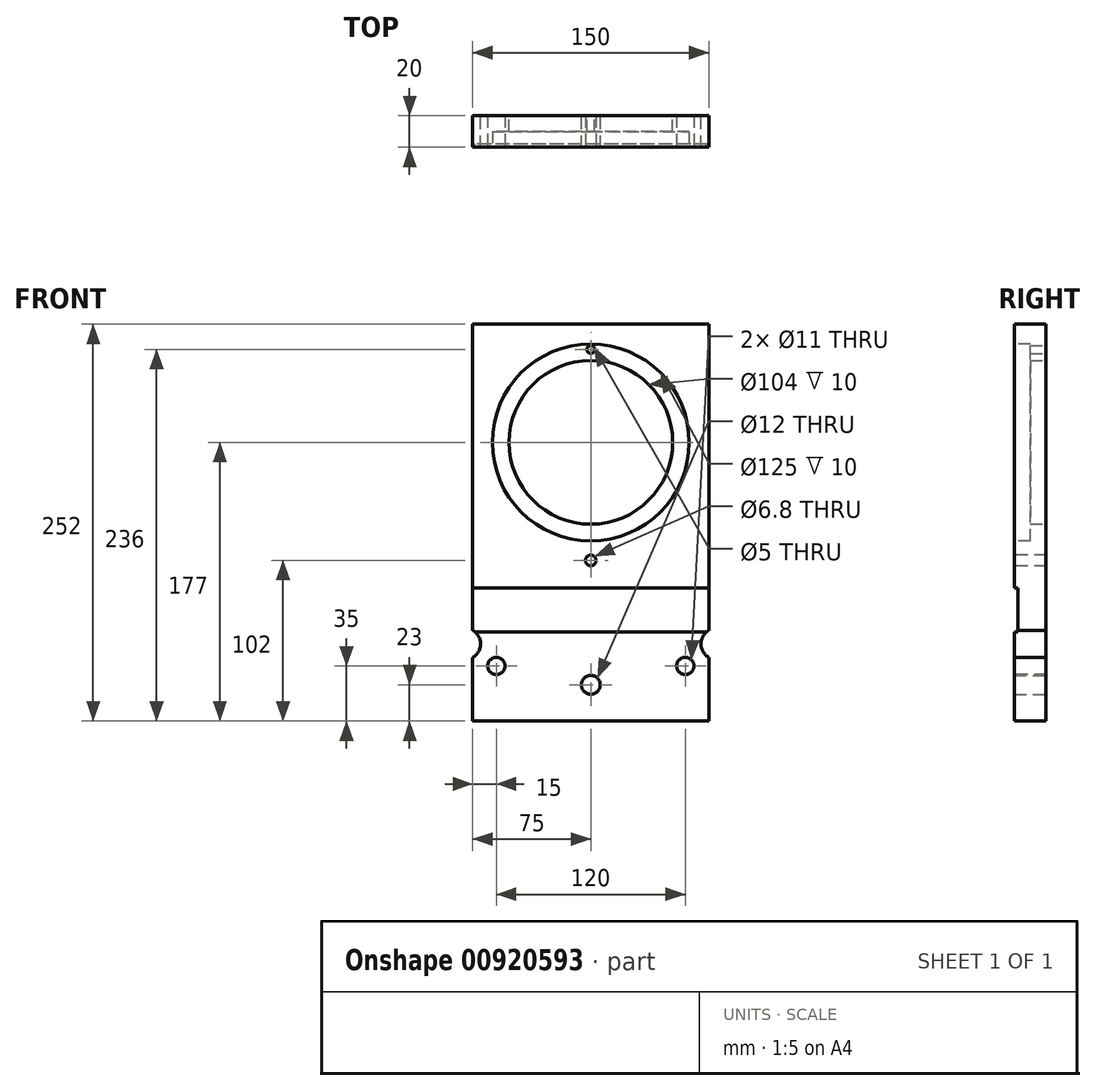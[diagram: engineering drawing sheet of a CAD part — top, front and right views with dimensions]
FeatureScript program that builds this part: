
annotation { "Feature Type Name" : "Feature", "Feature Type Description" : "" }
export const myFeature = defineFeature(function(context is Context, id is Id, definition is map)
    precondition{}
    {
        {
            var Q0;
            Q0=qCreatedBy(makeId("Front.planeOp"),FACE);
            var sketch = newSketch(context, id + "F0", { "sketchPlane" : qUnion([Q0])});
            skLineSegment(sketch, "E0.bottom", {"start": v(-75, -60) * mm, "end": v(-35, -60) * mm, "construction": true});
            skLineSegment(sketch, "E0.top", {"start": v(-75, 30) * mm, "end": v(75, 30) * mm});
            skLineSegment(sketch, "E0.left", {"start": v(-75, -60) * mm, "end": v(-75, 30) * mm});
            skLineSegment(sketch, "E0.right", {"start": v(75, -60) * mm, "end": v(75, 30) * mm});
            skLineSegment(sketch, "E1", {"start": v(-35, -60) * mm, "end": v(-35, -10) * mm, "construction": true});
            skLineSegment(sketch, "E2", {"start": v(-35, -10) * mm, "end": v(35, -10) * mm, "construction": true});
            skLineSegment(sketch, "E3", {"start": v(35, -10) * mm, "end": v(35, -60) * mm, "construction": true});
            skLineSegment(sketch, "E4.trimOffspring", {"start": v(35, -60) * mm, "end": v(75, -60) * mm, "construction": true});
            skLineSegment(sketch, "E5", {"start": v(-75, -60) * mm, "end": v(75, -60) * mm});
            skSolve(sketch);
        }
        {
            var Q0;
            Q0=makeQuery(id+"F0.imprint","IMPRINT",FACE,{"disambiguationData":[TD([[makeQuery(id+"F0.imprint","IMPRINT",EDGE,{"derivedFrom":sQuery(id+"F0.wireOp",EDGE,"E0.top")}),-1.0]])]});
            extrude(context, id + "F1", {"entities" : qUnion([Q0]), "depth" : 20 * mm, "offsetDistance" : 25 * mm});
        }
        {
            var Q0;
            Q0=makeQuery(id+"F1.opExtrude","CAP_FACE",FACE,{"disambiguationData":[OSD([sQuery(id+"F0.wireOp",EDGE,"E0.bottom"),sQuery(id+"F0.wireOp",EDGE,"E0.top"),sQuery(id+"F0.wireOp",EDGE,"E0.left"),sQuery(id+"F0.wireOp",EDGE,"E0.right"),sQuery(id+"F0.wireOp",EDGE,"E1"),sQuery(id+"F0.wireOp",EDGE,"E2"),sQuery(id+"F0.wireOp",EDGE,"E3"),sQuery(id+"F0.wireOp",EDGE,"E4.trimOffspring")])],"isStart":false});
            var sketch = newSketch(context, id + "F2", { "sketchPlane" : qUnion([Q0])});
            skCircle(sketch, "E6", {"center": v(-60, -45) * mm, "radius": 5.5 * mm});
            skCircle(sketch, "E7", {"center": v(60, -45) * mm, "radius": 5.5 * mm});
            skSolve(sketch);
        }
        {
            var Q0;
            Q0=makeQuery(id+"F2.imprint","IMPRINT",FACE,{"disambiguationData":[TD([[makeQuery(id+"F2.imprint","IMPRINT",EDGE,{"derivedFrom":sQuery(id+"F2.wireOp",EDGE,"E6")}),1.0]])]});
            var Q1;
            Q1=makeQuery(id+"F2.imprint","IMPRINT",FACE,{"disambiguationData":[TD([[makeQuery(id+"F2.imprint","IMPRINT",EDGE,{"derivedFrom":sQuery(id+"F2.wireOp",EDGE,"E7")}),1.0]])]});
            extrude(context, id + "F3", {"entities" : qUnion([Q0, Q1]), "operationType" : NewBodyOperationType.REMOVE, "endBound" : BoundingType.THROUGH_ALL, "oppositeDirection" : true, "depth" : 25 * mm, "offsetDistance" : 25 * mm});
        }
        {
            var Q0;
            Q0=makeQuery(id+"F1.opExtrude","SWEPT_FACE",FACE,{"disambiguationData":[OSD([sQuery(id+"F0.wireOp",EDGE,"E0.left")])]});
            var sketch = newSketch(context, id + "F4", { "sketchPlane" : qUnion([Q0])});
            skLineSegment(sketch, "E8.bottom", {"start": v(20, 4.5) * mm, "end": v(18, 4.5) * mm});
            skLineSegment(sketch, "E8.top", {"start": v(20, -23.5) * mm, "end": v(18, -23.5) * mm});
            skLineSegment(sketch, "E8.left", {"start": v(20, 4.5) * mm, "end": v(20, -23.5) * mm});
            skLineSegment(sketch, "E8.right", {"start": v(18, 4.5) * mm, "end": v(18, -23.5) * mm});
            skSolve(sketch);
        }
        {
            var Q0;
            Q0=makeQuery(id+"F4.imprint","IMPRINT",FACE,{"disambiguationData":[TD([[makeQuery(id+"F4.imprint","IMPRINT",EDGE,{"derivedFrom":sQuery(id+"F4.wireOp",EDGE,"E8.bottom")}),1.0]])]});
            extrude(context, id + "F5", {"entities" : qUnion([Q0]), "operationType" : NewBodyOperationType.REMOVE, "endBound" : BoundingType.THROUGH_ALL, "oppositeDirection" : true, "depth" : 25 * mm, "offsetDistance" : 25 * mm});
        }
        {
            var Q0;
            Q0=makeQuery(id+"F1.opExtrude","CAP_FACE",FACE,{"disambiguationData":[OSD([sQuery(id+"F0.wireOp",EDGE,"E0.bottom"),sQuery(id+"F0.wireOp",EDGE,"E0.top"),sQuery(id+"F0.wireOp",EDGE,"E0.left"),sQuery(id+"F0.wireOp",EDGE,"E0.right"),sQuery(id+"F0.wireOp",EDGE,"E1"),sQuery(id+"F0.wireOp",EDGE,"E2"),sQuery(id+"F0.wireOp",EDGE,"E3"),sQuery(id+"F0.wireOp",EDGE,"E4.trimOffspring")])],"isStart":true});
            var sketch = newSketch(context, id + "F6", { "sketchPlane" : qUnion([Q0])});
            skLineSegment(sketch, "E9", {"start": v(-75, 30) * mm, "end": v(-20, 154) * mm, "construction": true});
            skLineSegment(sketch, "E10", {"start": v(-75, 154) * mm, "end": v(75, 154) * mm});
            skLineSegment(sketch, "E11", {"start": v(20, 154) * mm, "end": v(75, 30) * mm, "construction": true});
            skLineSegment(sketch, "E12", {"start": v(75, 30) * mm, "end": v(-75, 30) * mm});
            skCircle(sketch, "E13", {"center": v(0, 97) * mm, "radius": 30 * mm});
            skLineSegment(sketch, "E14", {"start": v(75, 30) * mm, "end": v(75, 154) * mm});
            skLineSegment(sketch, "E15", {"start": v(-75, 30) * mm, "end": v(-75, 154) * mm});
            skSolve(sketch);
        }
        {
            var Q0;
            Q0=makeQuery(id+"F6.imprint","IMPRINT",FACE,{"disambiguationData":[TD([[makeQuery(id+"F6.imprint","IMPRINT",EDGE,{"derivedFrom":sQuery(id+"F6.wireOp",EDGE,"E10")}),-1.0]])]});
            extrude(context, id + "F7", {"entities" : qUnion([Q0]), "operationType" : NewBodyOperationType.ADD, "oppositeDirection" : true, "depth" : 20 * mm, "offsetDistance" : 25 * mm});
        }
        {
            var Q0;
            Q0=makeQuery(id+"F7.boolean.opBoolean","MERGE",FACE,{"derivedFrom":[makeQuery(id+"F1.opExtrude","CAP_FACE",FACE,{"disambiguationData":[OSD([sQuery(id+"F0.wireOp",EDGE,"E0.bottom"),sQuery(id+"F0.wireOp",EDGE,"E0.top"),sQuery(id+"F0.wireOp",EDGE,"E0.left"),sQuery(id+"F0.wireOp",EDGE,"E0.right"),sQuery(id+"F0.wireOp",EDGE,"E1"),sQuery(id+"F0.wireOp",EDGE,"E2"),sQuery(id+"F0.wireOp",EDGE,"E3"),sQuery(id+"F0.wireOp",EDGE,"E4.trimOffspring")])],"isStart":true}),makeQuery(id+"F7.opExtrude","CAP_FACE",FACE,{"disambiguationData":[OSD([sQuery(id+"F6.wireOp",EDGE,"E10"),sQuery(id+"F6.wireOp",EDGE,"E12"),sQuery(id+"F6.wireOp",EDGE,"E13"),sQuery(id+"F6.wireOp",EDGE,"E14"),sQuery(id+"F6.wireOp",EDGE,"E15")])],"isStart":true})]});
            var sketch = newSketch(context, id + "F8", { "sketchPlane" : qUnion([Q0])});
            skCircle(sketch, "E16", {"center": v(-80, -31) * mm, "radius": 10 * mm});
            skCircle(sketch, "E17", {"center": v(80, -31) * mm, "radius": 10 * mm});
            skSolve(sketch);
        }
        {
            var Q0;
            {var subQ0=sQuery(id+"F8.wireOp",EDGE,"E16");var subQ1=makeQuery(id+"F7.boolean.opBoolean","MERGE",EDGE,{"derivedFrom":[makeQuery(id+"F1.opExtrude","CAP_EDGE",EDGE,{"disambiguationData":[OSD([sQuery(id+"F0.wireOp",EDGE,"E0.right")])],"isStart":true}),makeQuery(id+"F7.opExtrude","CAP_EDGE",EDGE,{"disambiguationData":[OSD([sQuery(id+"F6.wireOp",EDGE,"E15")])],"isStart":true})]});var subQ2=makeQuery(id+"F8.imprint","INTERSECT",VERTEX,{"disambiguationData":[OD(0.0)],"derivedFrom":[subQ1,subQ0]});Q0=makeQuery(id+"F8.imprint","IMPRINT",FACE,{"disambiguationData":[TD([[makeQuery(id+"F8.imprint","IMPRINT",EDGE,{"disambiguationData":[TD([[subQ2,1.0]])],"derivedFrom":subQ0}),1.0]])]});}
            var Q1;
            {var subQ0=sQuery(id+"F8.wireOp",EDGE,"E16");var subQ1=makeQuery(id+"F7.boolean.opBoolean","MERGE",EDGE,{"derivedFrom":[makeQuery(id+"F1.opExtrude","CAP_EDGE",EDGE,{"disambiguationData":[OSD([sQuery(id+"F0.wireOp",EDGE,"E0.right")])],"isStart":true}),makeQuery(id+"F7.opExtrude","CAP_EDGE",EDGE,{"disambiguationData":[OSD([sQuery(id+"F6.wireOp",EDGE,"E15")])],"isStart":true})]});var subQ2=makeQuery(id+"F8.imprint","INTERSECT",VERTEX,{"disambiguationData":[OD(0.0)],"derivedFrom":[subQ1,subQ0]});Q1=makeQuery(id+"F8.imprint","IMPRINT",FACE,{"disambiguationData":[TD([[makeQuery(id+"F8.imprint","IMPRINT",EDGE,{"disambiguationData":[TD([[subQ2,-1.0]])],"derivedFrom":subQ0}),1.0]])]});}
            var Q2;
            {var subQ0=sQuery(id+"F8.wireOp",EDGE,"E17");var subQ1=makeQuery(id+"F7.boolean.opBoolean","MERGE",EDGE,{"derivedFrom":[makeQuery(id+"F1.opExtrude","CAP_EDGE",EDGE,{"disambiguationData":[OSD([sQuery(id+"F0.wireOp",EDGE,"E0.left")])],"isStart":true}),makeQuery(id+"F7.opExtrude","CAP_EDGE",EDGE,{"disambiguationData":[OSD([sQuery(id+"F6.wireOp",EDGE,"E14")])],"isStart":true})]});var subQ2=makeQuery(id+"F8.imprint","INTERSECT",VERTEX,{"disambiguationData":[OD(0.0)],"derivedFrom":[subQ1,subQ0]});Q2=makeQuery(id+"F8.imprint","IMPRINT",FACE,{"disambiguationData":[TD([[makeQuery(id+"F8.imprint","IMPRINT",EDGE,{"disambiguationData":[TD([[subQ2,1.0]])],"derivedFrom":subQ0}),1.0]])]});}
            var Q3;
            {var subQ0=sQuery(id+"F8.wireOp",EDGE,"E17");var subQ1=makeQuery(id+"F7.boolean.opBoolean","MERGE",EDGE,{"derivedFrom":[makeQuery(id+"F1.opExtrude","CAP_EDGE",EDGE,{"disambiguationData":[OSD([sQuery(id+"F0.wireOp",EDGE,"E0.left")])],"isStart":true}),makeQuery(id+"F7.opExtrude","CAP_EDGE",EDGE,{"disambiguationData":[OSD([sQuery(id+"F6.wireOp",EDGE,"E14")])],"isStart":true})]});var subQ2=makeQuery(id+"F8.imprint","INTERSECT",VERTEX,{"disambiguationData":[OD(0.0)],"derivedFrom":[subQ1,subQ0]});Q3=makeQuery(id+"F8.imprint","IMPRINT",FACE,{"disambiguationData":[TD([[makeQuery(id+"F8.imprint","IMPRINT",EDGE,{"disambiguationData":[TD([[subQ2,-1.0]])],"derivedFrom":subQ0}),1.0]])]});}
            extrude(context, id + "F9", {"entities" : qUnion([Q0, Q1, Q2, Q3]), "operationType" : NewBodyOperationType.REMOVE, "endBound" : BoundingType.THROUGH_ALL, "oppositeDirection" : true, "depth" : 25 * mm, "offsetDistance" : 25 * mm});
        }
        {
            var Q0;
            {var subQ0=sQuery(id+"F0.wireOp",EDGE,"E0.top");var subQ1=sQuery(id+"F0.wireOp",EDGE,"E0.left");var subQ2=sQuery(id+"F0.wireOp",EDGE,"E0.right");Q0=makeQuery(id+"F7.boolean.opBoolean","MERGE",FACE,{"derivedFrom":[makeQuery(id+"F5.boolean.opBoolean","SPLIT",FACE,{"disambiguationData":[TD([makeQuery(id+"F1.opExtrude","SWEPT_FACE",FACE,{"disambiguationData":[OSD([subQ0])]})])],"derivedFrom":makeQuery(id+"F1.opExtrude","CAP_FACE",FACE,{"disambiguationData":[OSD([subQ0,subQ1,subQ2,sQuery(id+"F0.wireOp",EDGE,"E5")])],"isStart":false})}),makeQuery(id+"F7.opExtrude","CAP_FACE",FACE,{"disambiguationData":[OSD([sQuery(id+"F6.wireOp",EDGE,"E10"),sQuery(id+"F6.wireOp",EDGE,"E12"),sQuery(id+"F6.wireOp",EDGE,"E13"),sQuery(id+"F6.wireOp",EDGE,"E14"),sQuery(id+"F6.wireOp",EDGE,"E15")])],"isStart":false})]});}
            var sketch = newSketch(context, id + "F10", { "sketchPlane" : qUnion([Q0])});
            skCircle(sketch, "E18.0", {"center": v(0, 97) * mm, "radius": 30 * mm, "construction": true});
            skLineSegment(sketch, "E19.bottom", {"start": v(-3.5, 146) * mm, "end": v(3.5, 146) * mm});
            skLineSegment(sketch, "E19.top", {"start": v(-3.5, 128) * mm, "end": v(3.5, 128) * mm});
            skLineSegment(sketch, "E19.left", {"start": v(-3.5, 146) * mm, "end": v(-3.5, 128) * mm});
            skLineSegment(sketch, "E19.right", {"start": v(3.5, 146) * mm, "end": v(3.5, 128) * mm});
            skLineSegment(sketch, "E20", {"start": v(-3.5, 137) * mm, "end": v(3.5, 137) * mm, "construction": true});
            skSolve(sketch);
        }
        {
            var Q0;
            Q0=makeQuery(id+"F7.boolean.opBoolean","MERGE",FACE,{"derivedFrom":[makeQuery(id+"F1.opExtrude","CAP_FACE",FACE,{"disambiguationData":[OSD([sQuery(id+"F0.wireOp",EDGE,"E0.top"),sQuery(id+"F0.wireOp",EDGE,"E0.left"),sQuery(id+"F0.wireOp",EDGE,"E0.right"),sQuery(id+"F0.wireOp",EDGE,"E5")])],"isStart":true}),makeQuery(id+"F7.opExtrude","CAP_FACE",FACE,{"disambiguationData":[OSD([sQuery(id+"F6.wireOp",EDGE,"E10"),sQuery(id+"F6.wireOp",EDGE,"E12"),sQuery(id+"F6.wireOp",EDGE,"E13"),sQuery(id+"F6.wireOp",EDGE,"E14"),sQuery(id+"F6.wireOp",EDGE,"E15")])],"isStart":true})]});
            var sketch = newSketch(context, id + "F11", { "sketchPlane" : qUnion([Q0])});
            skLineSegment(sketch, "E21.bottom", {"start": v(-75, -60) * mm, "end": v(75, -60) * mm});
            skLineSegment(sketch, "E21.top", {"start": v(-75, -80) * mm, "end": v(75, -80) * mm});
            skLineSegment(sketch, "E21.left", {"start": v(-75, -60) * mm, "end": v(-75, -80) * mm});
            skLineSegment(sketch, "E21.right", {"start": v(75, -60) * mm, "end": v(75, -80) * mm});
            skPoint(sketch, "E22.centerSnap0", {"position": v(0, -60) * mm});
            skSolve(sketch);
        }
        {
            var Q0;
            Q0=makeQuery(id+"F11.imprint","IMPRINT",FACE,{"disambiguationData":[TD([[makeQuery(id+"F11.imprint","IMPRINT",EDGE,{"derivedFrom":sQuery(id+"F11.wireOp",EDGE,"E21.bottom")}),1.0]])]});
            extrude(context, id + "F12", {"entities" : qUnion([Q0]), "operationType" : NewBodyOperationType.ADD, "oppositeDirection" : true, "depth" : 20 * mm, "offsetDistance" : 25 * mm});
        }
        {
            var Q0;
            Q0=makeQuery(id+"F12.boolean.opBoolean","MERGE",FACE,{"derivedFrom":[makeQuery(id+"F7.boolean.opBoolean","MERGE",FACE,{"derivedFrom":[makeQuery(id+"F1.opExtrude","CAP_FACE",FACE,{"disambiguationData":[OSD([sQuery(id+"F0.wireOp",EDGE,"E0.top"),sQuery(id+"F0.wireOp",EDGE,"E0.left"),sQuery(id+"F0.wireOp",EDGE,"E0.right"),sQuery(id+"F0.wireOp",EDGE,"E5")])],"isStart":true}),makeQuery(id+"F7.opExtrude","CAP_FACE",FACE,{"disambiguationData":[OSD([sQuery(id+"F6.wireOp",EDGE,"E10"),sQuery(id+"F6.wireOp",EDGE,"E12"),sQuery(id+"F6.wireOp",EDGE,"E13"),sQuery(id+"F6.wireOp",EDGE,"E14"),sQuery(id+"F6.wireOp",EDGE,"E15")])],"isStart":true})]}),makeQuery(id+"F12.opExtrude","CAP_FACE",FACE,{"disambiguationData":[OSD([sQuery(id+"F11.wireOp",EDGE,"E21.bottom"),sQuery(id+"F11.wireOp",EDGE,"E21.top"),sQuery(id+"F11.wireOp",EDGE,"E21.left"),sQuery(id+"F11.wireOp",EDGE,"E21.right")])],"isStart":true})]});
            var sketch = newSketch(context, id + "F13", { "sketchPlane" : qUnion([Q0])});
            skCircle(sketch, "E23", {"center": v(0, -57) * mm, "radius": 6 * mm});
            skCircle(sketch, "E24.0", {"center": v(0, 97) * mm, "radius": 30 * mm, "construction": true});
            skSolve(sketch);
        }
        {
            var Q0;
            Q0=makeQuery(id+"F13.imprint","IMPRINT",FACE,{"disambiguationData":[TD([[makeQuery(id+"F13.imprint","IMPRINT",EDGE,{"derivedFrom":sQuery(id+"F13.wireOp",EDGE,"E23")}),1.0]])]});
            extrude(context, id + "F14", {"entities" : qUnion([Q0]), "operationType" : NewBodyOperationType.REMOVE, "endBound" : BoundingType.THROUGH_ALL, "oppositeDirection" : true, "depth" : 25 * mm, "offsetDistance" : 25 * mm});
        }
        {
            var Q0;
            {var subQ0=sQuery(id+"F0.wireOp",EDGE,"E0.top");var subQ1=sQuery(id+"F0.wireOp",EDGE,"E0.left");var subQ2=sQuery(id+"F0.wireOp",EDGE,"E0.right");Q0=makeQuery(id+"F7.boolean.opBoolean","MERGE",FACE,{"derivedFrom":[makeQuery(id+"F5.boolean.opBoolean","SPLIT",FACE,{"disambiguationData":[TD([makeQuery(id+"F1.opExtrude","SWEPT_FACE",FACE,{"disambiguationData":[OSD([subQ0])]})])],"derivedFrom":makeQuery(id+"F1.opExtrude","CAP_FACE",FACE,{"disambiguationData":[OSD([subQ0,subQ1,subQ2,sQuery(id+"F0.wireOp",EDGE,"E5")])],"isStart":false})}),makeQuery(id+"F7.opExtrude","CAP_FACE",FACE,{"disambiguationData":[OSD([sQuery(id+"F6.wireOp",EDGE,"E10"),sQuery(id+"F6.wireOp",EDGE,"E12"),sQuery(id+"F6.wireOp",EDGE,"E13"),sQuery(id+"F6.wireOp",EDGE,"E14"),sQuery(id+"F6.wireOp",EDGE,"E15")])],"isStart":false})]});}
            var sketch = newSketch(context, id + "F15", { "sketchPlane" : qUnion([Q0])});
            skLineSegment(sketch, "E25.bottom", {"start": v(-75, 154) * mm, "end": v(75, 154) * mm});
            skLineSegment(sketch, "E25.top", {"start": v(-75, 172) * mm, "end": v(75, 172) * mm});
            skLineSegment(sketch, "E25.left", {"start": v(-75, 154) * mm, "end": v(-75, 172) * mm});
            skLineSegment(sketch, "E25.right", {"start": v(75, 154) * mm, "end": v(75, 172) * mm});
            skSolve(sketch);
        }
        {
            var Q0;
            Q0=makeQuery(id+"F15.imprint","IMPRINT",FACE,{"disambiguationData":[TD([[makeQuery(id+"F15.imprint","IMPRINT",EDGE,{"derivedFrom":sQuery(id+"F15.wireOp",EDGE,"E25.bottom")}),-1.0]])]});
            extrude(context, id + "F16", {"entities" : qUnion([Q0]), "operationType" : NewBodyOperationType.ADD, "oppositeDirection" : true, "depth" : 20 * mm, "offsetDistance" : 25 * mm});
        }
        {
            var Q0;
            Q0=makeQuery(id+"F16.boolean.opBoolean","MERGE",FACE,{"derivedFrom":[makeQuery(id+"F12.boolean.opBoolean","MERGE",FACE,{"derivedFrom":[makeQuery(id+"F7.boolean.opBoolean","MERGE",FACE,{"derivedFrom":[makeQuery(id+"F1.opExtrude","CAP_FACE",FACE,{"disambiguationData":[OSD([sQuery(id+"F0.wireOp",EDGE,"E0.top"),sQuery(id+"F0.wireOp",EDGE,"E0.left"),sQuery(id+"F0.wireOp",EDGE,"E0.right"),sQuery(id+"F0.wireOp",EDGE,"E5")])],"isStart":true}),makeQuery(id+"F7.opExtrude","CAP_FACE",FACE,{"disambiguationData":[OSD([sQuery(id+"F6.wireOp",EDGE,"E10"),sQuery(id+"F6.wireOp",EDGE,"E12"),sQuery(id+"F6.wireOp",EDGE,"E13"),sQuery(id+"F6.wireOp",EDGE,"E14"),sQuery(id+"F6.wireOp",EDGE,"E15")])],"isStart":true})]}),makeQuery(id+"F12.opExtrude","CAP_FACE",FACE,{"disambiguationData":[OSD([sQuery(id+"F11.wireOp",EDGE,"E21.bottom"),sQuery(id+"F11.wireOp",EDGE,"E21.top"),sQuery(id+"F11.wireOp",EDGE,"E21.left"),sQuery(id+"F11.wireOp",EDGE,"E21.right")])],"isStart":true})]}),makeQuery(id+"F16.opExtrude","CAP_FACE",FACE,{"disambiguationData":[OSD([sQuery(id+"F15.wireOp",EDGE,"E25.bottom"),sQuery(id+"F15.wireOp",EDGE,"E25.top"),sQuery(id+"F15.wireOp",EDGE,"E25.left"),sQuery(id+"F15.wireOp",EDGE,"E25.right")])],"isStart":false})]});
            var sketch = newSketch(context, id + "F17", { "sketchPlane" : qUnion([Q0])});
            skCircle(sketch, "E26", {"center": v(0, 97) * mm, "radius": 52 * mm});
            skSolve(sketch);
        }
        {
            var Q0;
            Q0=makeQuery(id+"F17.imprint","IMPRINT",FACE,{"disambiguationData":[TD([[makeQuery(id+"F17.imprint","IMPRINT",EDGE,{"derivedFrom":sQuery(id+"F17.wireOp",EDGE,"E26")}),1.0]])]});
            extrude(context, id + "F18", {"entities" : qUnion([Q0]), "operationType" : NewBodyOperationType.REMOVE, "oppositeDirection" : true, "depth" : 20 * mm, "offsetDistance" : 25 * mm});
        }
        {
            var Q0;
            Q0=makeQuery(id+"F16.boolean.opBoolean","MERGE",FACE,{"derivedFrom":[makeQuery(id+"F12.boolean.opBoolean","MERGE",FACE,{"derivedFrom":[makeQuery(id+"F7.boolean.opBoolean","MERGE",FACE,{"derivedFrom":[makeQuery(id+"F1.opExtrude","CAP_FACE",FACE,{"disambiguationData":[OSD([sQuery(id+"F0.wireOp",EDGE,"E0.top"),sQuery(id+"F0.wireOp",EDGE,"E0.left"),sQuery(id+"F0.wireOp",EDGE,"E0.right"),sQuery(id+"F0.wireOp",EDGE,"E5")])],"isStart":true}),makeQuery(id+"F7.opExtrude","CAP_FACE",FACE,{"disambiguationData":[OSD([sQuery(id+"F6.wireOp",EDGE,"E10"),sQuery(id+"F6.wireOp",EDGE,"E12"),sQuery(id+"F6.wireOp",EDGE,"E13"),sQuery(id+"F6.wireOp",EDGE,"E14"),sQuery(id+"F6.wireOp",EDGE,"E15")])],"isStart":true})]}),makeQuery(id+"F12.opExtrude","CAP_FACE",FACE,{"disambiguationData":[OSD([sQuery(id+"F11.wireOp",EDGE,"E21.bottom"),sQuery(id+"F11.wireOp",EDGE,"E21.top"),sQuery(id+"F11.wireOp",EDGE,"E21.left"),sQuery(id+"F11.wireOp",EDGE,"E21.right")])],"isStart":true})]}),makeQuery(id+"F16.opExtrude","CAP_FACE",FACE,{"disambiguationData":[OSD([sQuery(id+"F15.wireOp",EDGE,"E25.bottom"),sQuery(id+"F15.wireOp",EDGE,"E25.top"),sQuery(id+"F15.wireOp",EDGE,"E25.left"),sQuery(id+"F15.wireOp",EDGE,"E25.right")])],"isStart":false})]});
            var sketch = newSketch(context, id + "F19", { "sketchPlane" : qUnion([Q0])});
            skLineSegment(sketch, "E27.bottom", {"start": v(-75, -80) * mm, "end": v(75, -80) * mm});
            skLineSegment(sketch, "E27.top", {"start": v(-75, -113.5) * mm, "end": v(75, -113.5) * mm});
            skLineSegment(sketch, "E27.left", {"start": v(-75, -80) * mm, "end": v(-75, -113.5) * mm});
            skLineSegment(sketch, "E27.right", {"start": v(75, -80) * mm, "end": v(75, -113.5) * mm});
            skSolve(sketch);
        }
        {
            var Q0;
            {var subQ0=sQuery(id+"F0.wireOp",EDGE,"E0.top");var subQ1=sQuery(id+"F0.wireOp",EDGE,"E0.left");var subQ2=sQuery(id+"F0.wireOp",EDGE,"E0.right");Q0=makeQuery(id+"F16.boolean.opBoolean","MERGE",FACE,{"derivedFrom":[makeQuery(id+"F7.boolean.opBoolean","MERGE",FACE,{"derivedFrom":[makeQuery(id+"F5.boolean.opBoolean","SPLIT",FACE,{"disambiguationData":[TD([makeQuery(id+"F1.opExtrude","SWEPT_FACE",FACE,{"disambiguationData":[OSD([subQ0])]})])],"derivedFrom":makeQuery(id+"F1.opExtrude","CAP_FACE",FACE,{"disambiguationData":[OSD([subQ0,subQ1,subQ2,sQuery(id+"F0.wireOp",EDGE,"E5")])],"isStart":false})}),makeQuery(id+"F7.opExtrude","CAP_FACE",FACE,{"disambiguationData":[OSD([sQuery(id+"F6.wireOp",EDGE,"E10"),sQuery(id+"F6.wireOp",EDGE,"E12"),sQuery(id+"F6.wireOp",EDGE,"E13"),sQuery(id+"F6.wireOp",EDGE,"E14"),sQuery(id+"F6.wireOp",EDGE,"E15")])],"isStart":false})]}),makeQuery(id+"F16.opExtrude","CAP_FACE",FACE,{"disambiguationData":[OSD([sQuery(id+"F15.wireOp",EDGE,"E25.bottom"),sQuery(id+"F15.wireOp",EDGE,"E25.top"),sQuery(id+"F15.wireOp",EDGE,"E25.left"),sQuery(id+"F15.wireOp",EDGE,"E25.right")])],"isStart":true})]});}
            var sketch = newSketch(context, id + "F20", { "sketchPlane" : qUnion([Q0])});
            skCircle(sketch, "E28", {"center": v(0, 97) * mm, "radius": 62.5 * mm});
            skSolve(sketch);
        }
        {
            var Q0;
            Q0=makeQuery(id+"F20.imprint","IMPRINT",FACE,{"disambiguationData":[TD([[makeQuery(id+"F20.imprint","IMPRINT",EDGE,{"derivedFrom":sQuery(id+"F20.wireOp",EDGE,"E28")}),1.0]])]});
            extrude(context, id + "F21", {"entities" : qUnion([Q0]), "operationType" : NewBodyOperationType.REMOVE, "oppositeDirection" : true, "depth" : 10 * mm, "offsetDistance" : 25 * mm});
        }
        {
            var Q0;
            {var subQ0=sQuery(id+"F0.wireOp",EDGE,"E0.top");var subQ1=sQuery(id+"F0.wireOp",EDGE,"E0.left");var subQ2=sQuery(id+"F0.wireOp",EDGE,"E0.right");Q0=makeQuery(id+"F16.boolean.opBoolean","MERGE",FACE,{"derivedFrom":[makeQuery(id+"F7.boolean.opBoolean","MERGE",FACE,{"derivedFrom":[makeQuery(id+"F5.boolean.opBoolean","SPLIT",FACE,{"disambiguationData":[TD([makeQuery(id+"F1.opExtrude","SWEPT_FACE",FACE,{"disambiguationData":[OSD([subQ0])]})])],"derivedFrom":makeQuery(id+"F1.opExtrude","CAP_FACE",FACE,{"disambiguationData":[OSD([subQ0,subQ1,subQ2,sQuery(id+"F0.wireOp",EDGE,"E5")])],"isStart":false})}),makeQuery(id+"F7.opExtrude","CAP_FACE",FACE,{"disambiguationData":[OSD([sQuery(id+"F6.wireOp",EDGE,"E10"),sQuery(id+"F6.wireOp",EDGE,"E12"),sQuery(id+"F6.wireOp",EDGE,"E13"),sQuery(id+"F6.wireOp",EDGE,"E14"),sQuery(id+"F6.wireOp",EDGE,"E15")])],"isStart":false})]}),makeQuery(id+"F16.opExtrude","CAP_FACE",FACE,{"disambiguationData":[OSD([sQuery(id+"F15.wireOp",EDGE,"E25.bottom"),sQuery(id+"F15.wireOp",EDGE,"E25.top"),sQuery(id+"F15.wireOp",EDGE,"E25.left"),sQuery(id+"F15.wireOp",EDGE,"E25.right")])],"isStart":true})]});}
            var sketch = newSketch(context, id + "F22", { "sketchPlane" : qUnion([Q0])});
            skCircle(sketch, "E29", {"center": v(0, 22) * mm, "radius": 3.4 * mm});
            skCircle(sketch, "E30.0", {"center": v(0, 97) * mm, "radius": 62.5 * mm, "construction": true});
            skSolve(sketch);
        }
        {
            var Q0;
            Q0=makeQuery(id+"F22.imprint","IMPRINT",FACE,{"disambiguationData":[TD([[makeQuery(id+"F22.imprint","IMPRINT",EDGE,{"derivedFrom":sQuery(id+"F22.wireOp",EDGE,"E29")}),1.0]])]});
            extrude(context, id + "F23", {"entities" : qUnion([Q0]), "operationType" : NewBodyOperationType.REMOVE, "endBound" : BoundingType.THROUGH_ALL, "oppositeDirection" : true, "depth" : 25 * mm, "offsetDistance" : 25 * mm});
        }
        {
            var Q0;
            Q0=makeQuery(id+"FQzN8Jtf8JKBu59_1.boolean.opBoolean","MERGE",FACE,{"derivedFrom":[makeQuery(id+"F16.boolean.opBoolean","MERGE",FACE,{"derivedFrom":[makeQuery(id+"F12.boolean.opBoolean","MERGE",FACE,{"derivedFrom":[makeQuery(id+"F7.boolean.opBoolean","MERGE",FACE,{"derivedFrom":[makeQuery(id+"F1.opExtrude","CAP_FACE",FACE,{"disambiguationData":[OSD([sQuery(id+"F0.wireOp",EDGE,"E0.top"),sQuery(id+"F0.wireOp",EDGE,"E0.left"),sQuery(id+"F0.wireOp",EDGE,"E0.right"),sQuery(id+"F0.wireOp",EDGE,"E5")])],"isStart":true}),makeQuery(id+"F7.opExtrude","CAP_FACE",FACE,{"disambiguationData":[OSD([sQuery(id+"F6.wireOp",EDGE,"E10"),sQuery(id+"F6.wireOp",EDGE,"E12"),sQuery(id+"F6.wireOp",EDGE,"E13"),sQuery(id+"F6.wireOp",EDGE,"E14"),sQuery(id+"F6.wireOp",EDGE,"E15")])],"isStart":true})]}),makeQuery(id+"F12.opExtrude","CAP_FACE",FACE,{"disambiguationData":[OSD([sQuery(id+"F11.wireOp",EDGE,"E21.bottom"),sQuery(id+"F11.wireOp",EDGE,"E21.top"),sQuery(id+"F11.wireOp",EDGE,"E21.left"),sQuery(id+"F11.wireOp",EDGE,"E21.right")])],"isStart":true})]}),makeQuery(id+"F16.opExtrude","CAP_FACE",FACE,{"disambiguationData":[OSD([sQuery(id+"F15.wireOp",EDGE,"E25.bottom"),sQuery(id+"F15.wireOp",EDGE,"E25.top"),sQuery(id+"F15.wireOp",EDGE,"E25.left"),sQuery(id+"F15.wireOp",EDGE,"E25.right")])],"isStart":false})]}),makeQuery(id+"FQzN8Jtf8JKBu59_1.opExtrude","CAP_FACE",FACE,{"disambiguationData":[OSD([sQuery(id+"F19.wireOp",EDGE,"E27.bottom"),sQuery(id+"F19.wireOp",EDGE,"E27.top"),sQuery(id+"F19.wireOp",EDGE,"E27.left"),sQuery(id+"F19.wireOp",EDGE,"E27.right")])],"isStart":true})]});
            var sketch = newSketch(context, id + "F24", { "sketchPlane" : qUnion([Q0])});
            skCircle(sketch, "E31", {"center": v(0, 156) * mm, "radius": 2.5 * mm});
            skCircle(sketch, "E32.0", {"center": v(0, 97) * mm, "radius": 52 * mm});
            skSolve(sketch);
        }
        {
            var Q0;
            {var subQ0=sQuery(id+"F24.wireOp",EDGE,"E32.0");var subQ1=sQuery(id+"F24.wireOp",EDGE,"E31");var subQ2=makeQuery(id+"F24.imprint","INTERSECT",VERTEX,{"disambiguationData":[OD(0.0)],"derivedFrom":[subQ1,subQ0]});Q0=makeQuery(id+"F24.imprint","IMPRINT",FACE,{"disambiguationData":[TD([[makeQuery(id+"F24.imprint","IMPRINT",EDGE,{"disambiguationData":[TD([[subQ2,-1.0]])],"derivedFrom":subQ1}),1.0]])]});}
            var Q1;
            {var subQ0=sQuery(id+"F24.wireOp",EDGE,"E32.0");var subQ1=sQuery(id+"F24.wireOp",EDGE,"E31");var subQ2=makeQuery(id+"F24.imprint","INTERSECT",VERTEX,{"disambiguationData":[OD(0.0)],"derivedFrom":[subQ1,subQ0]});Q1=makeQuery(id+"F24.imprint","IMPRINT",FACE,{"disambiguationData":[TD([[makeQuery(id+"F24.imprint","IMPRINT",EDGE,{"disambiguationData":[TD([[subQ2,1.0]])],"derivedFrom":subQ1}),1.0]])]});}
            extrude(context, id + "F25", {"entities" : qUnion([Q0, Q1]), "operationType" : NewBodyOperationType.REMOVE, "endBound" : BoundingType.THROUGH_ALL, "oppositeDirection" : true, "depth" : 25 * mm, "offsetDistance" : 25 * mm});
        }
    });
